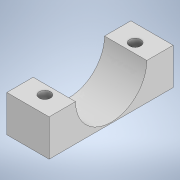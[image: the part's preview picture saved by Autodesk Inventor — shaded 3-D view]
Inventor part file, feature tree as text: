
AUTODESK INVENTOR PART (.ipt)
format: ipt  version: 2020 (Build 240168000, 168)  size: 114,176 bytes
history: native  units: mm
features: extrude x2, sketch x2, other x1
ambient origin geometry x8: Origin, YZ Plane, XZ Plane, XY Plane, X Axis, Y Axis, Z Axis, Center Point
bodies: Body1 (feature_tree)
feature tree (5):
  other  "Твердое тело1"
  extrude  "Выдавливание1"  Depth=15.0mm
  extrude  "Выдавливание2"  Depth=44.0mm
  sketch  "Эскиз1"
  sketch  "Эскиз2"
